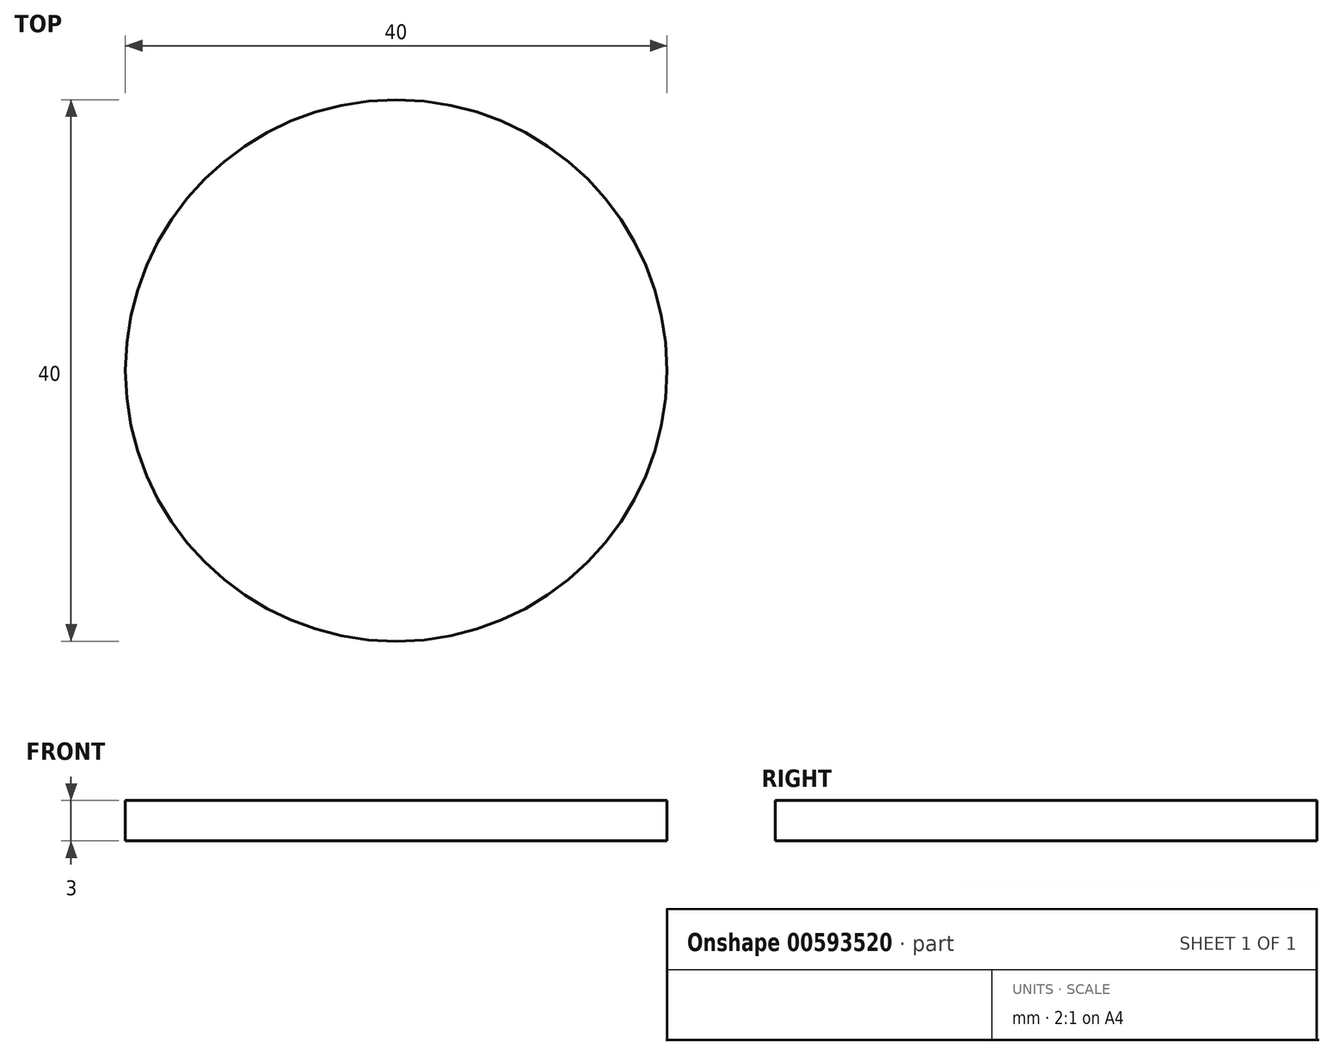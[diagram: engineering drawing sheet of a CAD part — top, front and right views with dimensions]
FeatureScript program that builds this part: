
annotation { "Feature Type Name" : "Feature", "Feature Type Description" : "" }
export const myFeature = defineFeature(function(context is Context, id is Id, definition is map)
    precondition{}
    {
        {
            var Q0;
            Q0=qCreatedBy(makeId("Top.planeOp"),FACE);
            var sketch = newSketch(context, id + "F0", { "sketchPlane" : qUnion([Q0])});
            skCircle(sketch, "E0", {"center": v(0, 0) * mm, "radius": 20 * mm});
            skSolve(sketch);
        }
        {
            var Q0;
            Q0 = qSketchRegion(id + "F0", true);
            extrude(context, id + "F1", {"entities" : qUnion([Q0]), "depth" : 3 * mm, "offsetDistance" : 25 * mm});
        }
    });
